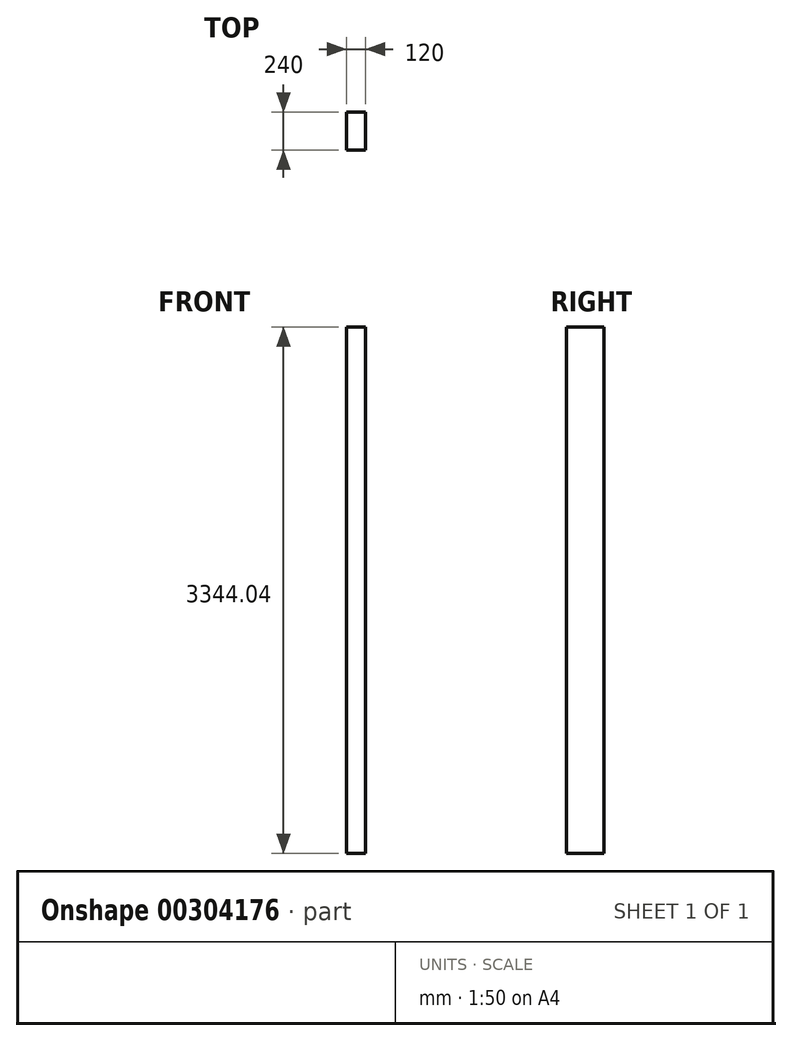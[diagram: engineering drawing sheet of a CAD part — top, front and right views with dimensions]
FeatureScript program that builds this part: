
annotation { "Feature Type Name" : "Feature", "Feature Type Description" : "" }
export const myFeature = defineFeature(function(context is Context, id is Id, definition is map)
    precondition{}
    {
        {
            var Q0;
            Q0=qCreatedBy(makeId("Top.planeOp"),FACE);
            var sketch = newSketch(context, id + "F0", { "sketchPlane" : qUnion([Q0])});
            skLineSegment(sketch, "E0.bottom", {"start": v(-67.42, 136.33) * mm, "end": v(52.58, 136.33) * mm});
            skLineSegment(sketch, "E0.top", {"start": v(-67.42, -103.67) * mm, "end": v(52.58, -103.67) * mm});
            skLineSegment(sketch, "E0.left", {"start": v(-67.42, 136.33) * mm, "end": v(-67.42, -103.67) * mm});
            skLineSegment(sketch, "E0.right", {"start": v(52.58, 136.33) * mm, "end": v(52.58, -103.67) * mm});
            skSolve(sketch);
        }
        {
            var Q0;
            Q0=makeQuery(id+"F0.imprint","IMPRINT",FACE,{"disambiguationData":[TD([[makeQuery(id+"F0.imprint","IMPRINT",EDGE,{"derivedFrom":sQuery(id+"F0.wireOp",EDGE,"E0.bottom")}),-1.0]])]});
            extrude(context, id + "F1", {"entities" : qUnion([Q0]), "depth" : 3344.04 * mm});
        }
    });
